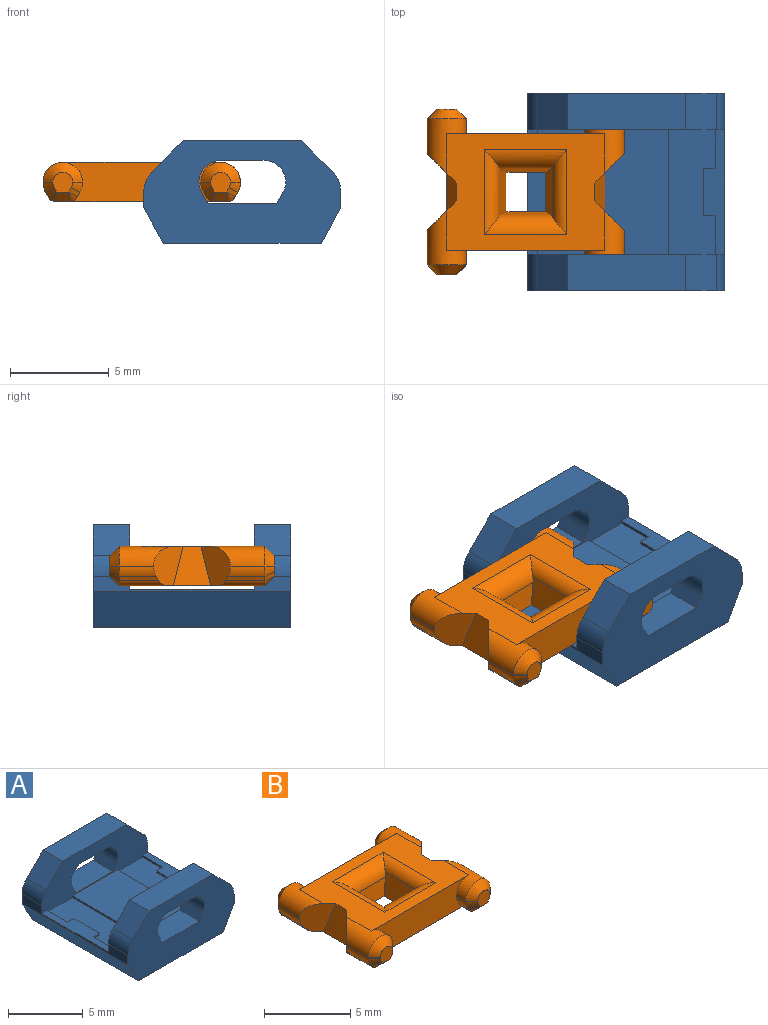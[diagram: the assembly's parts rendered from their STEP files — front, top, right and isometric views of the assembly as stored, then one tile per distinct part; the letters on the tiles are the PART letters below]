
ASSEMBLY  parts=2 mates=1
PART A: 48 faces, bbox 10x10x5.2 mm
  f0: plane 6.3x4.25mm, normal (0,0,1), area 26.8mm2, adj f4,f5,f38,f41
  f1: plane 6.3x1.1mm, normal (0,0,1), area 4.6mm2, adj f4,f5,f10,f42,f43,f44,f45,f46
  f2: plane 3.48x1.85mm, normal (0,0,1), area 6.4mm2, adj f5,f11,f25,f27
  f3: plane 10x0.78mm, normal (1,0,0), area 3.8mm2, adj f4,f5,f9,f11,f20,f29,f32,f33
  f4: plane 10x3.41mm, normal (0,-1,0), area 20.4mm2, adj f0,f1,f3,f7,f8,f10,f13,f17
  f5: plane 10x3.41mm, normal (0,1,0), area 20.4mm2, adj f0,f1,f2,f3,f6,f10,f14,f15
  f6: cylinder r=1.1mm len=1.85mm, axis (0,-1,0), area 4.2mm2, adj f5,f11,f16,f27
  f7: cylinder r=1.1mm len=1.85mm, axis (0,-1,0), area 4.2mm2, adj f4,f9,f17,f28
  f8: plane 3.48x1.85mm, normal (0,0,1), area 6.4mm2, adj f4,f9,f26,f28
  f9: plane 10x5.2mm, normal (0,1,0), area 37.3mm2, adj f3,f7,f8,f10,f12,f13,f17,f18
  f10: plane 10x0.78mm, normal (-1,0,0), area 3.8mm2, adj f1,f4,f5,f9,f11,f19,f30,f31
  f11: plane 10x5.2mm, normal (0,-1,0), area 37.3mm2, adj f2,f3,f6,f10,f12,f14,f15,f16
  f12: plane 10x8mm, normal (0,0,-1), area 80mm2, adj f9,f11,f19,f20
  f13: plane 6x1.85mm, normal (0,0,1), area 11.1mm2, adj f4,f9,f21,f23
  f14: plane 6x1.85mm, normal (0,0,1), area 11.1mm2, adj f5,f11,f22,f24
  f15: cylinder r=1.1mm len=1.85mm, axis (0,-1,0), area 4.2mm2, adj f5,f11,f16,f25
  f16: plane 2.2x1.85mm, normal (0,0,-1), area 4.1mm2, adj f5,f6,f11,f15
  f17: plane 2.2x1.85mm, normal (0,0,-1), area 4.1mm2, adj f4,f7,f9,f18
  f18: cylinder r=1.1mm len=1.85mm, axis (0,-1,0), area 4.2mm2, adj f4,f9,f17,f26
  f19: plane 10x1.8mm, normal (-0.87,0,-0.49), area 20.6mm2, adj f9,f10,f11,f12
  f20: plane 10x1.8mm, normal (0.87,0,-0.49), area 20.6mm2, adj f3,f9,f11,f12
  f21: plane 1.85x1.56mm, normal (0.71,0,0.71), area 4.1mm2, adj f4,f9,f13,f32
  f22: plane 1.85x1.56mm, normal (0.71,0,0.71), area 4.1mm2, adj f5,f11,f14,f33
  f23: plane 1.85x1.56mm, normal (-0.71,0,0.71), area 4.1mm2, adj f4,f9,f13,f30
  f24: plane 1.85x1.56mm, normal (-0.71,0,0.71), area 4.1mm2, adj f5,f11,f14,f31
  f25: plane 1.85x0.56mm, normal (0.87,0,0.5), area 1.2mm2, adj f2,f5,f11,f15
  f26: plane 1.85x0.56mm, normal (0.87,0,0.5), area 1.2mm2, adj f4,f8,f9,f18
  f27: plane 1.85x0.56mm, normal (-0.87,0,0.5), area 1.2mm2, adj f2,f5,f6,f11
  f28: plane 1.85x0.56mm, normal (-0.87,0,0.5), area 1.2mm2, adj f4,f7,f8,f9
  f29: plane 6.3x1.1mm, normal (0,0,1), area 4.6mm2, adj f3,f4,f5,f34,f35,f36,f37,f39
  f30: cylinder r=1.5mm len=1.85mm, axis (0,-1,0), area 2.2mm2, adj f4,f9,f10,f23
  f31: cylinder r=1.5mm len=1.85mm, axis (0,-1,0), area 2.2mm2, adj f5,f10,f11,f24
  f32: cylinder r=1.5mm len=1.85mm, axis (0,1,0), area 2.2mm2, adj f3,f4,f9,f21
  f33: cylinder r=1.5mm len=1.85mm, axis (0,1,0), area 2.2mm2, adj f3,f5,f11,f22
  f34: plane 0.6x0.15mm, normal (0,-1,0), area 0.1mm2, adj f29,f35,f39,f40
  f35: plane 2.4x0.15mm, normal (-1,0,0), area 0.4mm2, adj f29,f34,f36,f40
  f36: plane 0.6x0.15mm, normal (0,1,0), area 0.1mm2, adj f29,f35,f37,f40
  f37: plane 1.95x0.15mm, normal (-1,0,0), area 0.3mm2, adj f4,f29,f36,f40
  f38: plane 6.3x0.15mm, normal (1,0,0), area 0.9mm2, adj f0,f4,f5,f40
  f39: plane 1.95x0.15mm, normal (-1,0,0), area 0.3mm2, adj f5,f29,f34,f40
  f40: plane 6.3x2.38mm, normal (0,0,1), area 13.5mm2, adj f4,f5,f34,f35,f36,f37,f38,f39
  f41: plane 6.3x0.15mm, normal (-1,0,0), area 0.9mm2, adj f0,f4,f5,f47
  f42: plane 1.95x0.15mm, normal (1,0,0), area 0.3mm2, adj f1,f4,f43,f47
  f43: plane 0.6x0.15mm, normal (0,1,0), area 0.1mm2, adj f1,f42,f44,f47
  f44: plane 2.4x0.15mm, normal (1,0,0), area 0.4mm2, adj f1,f43,f45,f47
  f45: plane 0.6x0.15mm, normal (0,-1,0), area 0.1mm2, adj f1,f44,f46,f47
  f46: plane 1.95x0.15mm, normal (1,0,0), area 0.3mm2, adj f1,f5,f45,f47
  f47: plane 6.3x2.38mm, normal (0,0,1), area 13.5mm2, adj f4,f5,f41,f42,f43,f44,f45,f46
PART B: 98 faces, bbox 10x8.4x2 mm
  f0: plane 8x2mm, normal (0,1,0), area 12.7mm2, adj f2,f3,f10,f14,f20,f21,f24,f25
  f1: plane 8x2mm, normal (0,-1,0), area 12.7mm2, adj f2,f3,f4,f7,f22,f23,f28,f29
  f2: plane 8x5.9mm, normal (0,0,1), area 27.8mm2, adj f0,f1,f16,f17,f18,f19,f20,f21
  f3: plane 8.62x7.4mm, normal (0,0,-1), area 47.3mm2, adj f0,f1,f16,f17,f18,f19,f40,f41
  f4: plane 0.75x0.03mm, normal (1,0,0), area 0mm2, adj f1,f23,f35,f63
  f5: plane 1.75x0.03mm, normal (-1,0,0), area 0.1mm2, adj f18,f23,f36,f67
  f6: plane 1x1mm, normal (0,-1,0), area 0.8mm2, adj f62,f63,f64,f65,f67,f68,f69,f71
  f7: plane 0.75x0.03mm, normal (-1,0,0), area 0mm2, adj f1,f22,f34,f57
  f8: plane 1.75x0.03mm, normal (1,0,0), area 0.1mm2, adj f16,f22,f32,f53
  f9: plane 1x1mm, normal (0,-1,0), area 0.8mm2, adj f52,f53,f54,f55,f57,f58,f59,f61
  f10: plane 0.75x0.03mm, normal (1,0,0), area 0mm2, adj f0,f21,f38,f87
  f11: plane 1.75x0.03mm, normal (-1,0,0), area 0.1mm2, adj f19,f21,f37,f83
  f12: plane 1x1mm, normal (0,1,0), area 0.8mm2, adj f82,f83,f84,f85,f87,f88,f89,f91
  f13: plane 1.75x0.03mm, normal (1,0,0), area 0.1mm2, adj f17,f20,f33,f77
  f14: plane 0.75x0.03mm, normal (-1,0,0), area 0mm2, adj f0,f20,f39,f73
  f15: plane 1x1mm, normal (0,1,0), area 0.8mm2, adj f72,f73,f74,f75,f77,f78,f79,f81
  f16: plane 2x1.5mm, normal (0.71,0.71,0), area 3mm2, adj f2,f3,f8,f22,f31,f32,f47,f48
  f17: plane 2x1.5mm, normal (0.71,-0.71,0), area 3mm2, adj f2,f3,f13,f20,f30,f33,f46,f48
  f18: plane 2x1.5mm, normal (-0.71,0.71,0), area 3mm2, adj f2,f3,f5,f23,f27,f36,f43,f51
  f19: plane 2x1.5mm, normal (-0.71,-0.71,0), area 3mm2, adj f2,f3,f11,f21,f26,f37,f42,f51
  f20: cylinder r=1mm len=2.75mm, axis (0,-1,0), area 4.5mm2, adj f0,f2,f13,f14,f17,f75
  f21: cylinder r=1mm len=2.75mm, axis (0,-1,0), area 4.5mm2, adj f0,f2,f10,f11,f19,f85
  f22: cylinder r=1mm len=2.75mm, axis (0,-1,0), area 4.5mm2, adj f1,f2,f7,f8,f16,f55
  f23: cylinder r=1mm len=2.75mm, axis (0,-1,0), area 4.5mm2, adj f1,f2,f4,f5,f18,f65
  f24: plane 0.75x0.22mm, normal (-0.87,0,-0.5), area 0.2mm2, adj f0,f39,f40,f74
  f25: plane 0.75x0.22mm, normal (0.87,0,-0.5), area 0.2mm2, adj f0,f38,f41,f91
  f26: plane 2.01x0.22mm, normal (-0.87,0,-0.5), area 0.5mm2, adj f19,f37,f42,f84
  f27: plane 2.01x0.22mm, normal (-0.87,0,-0.5), area 0.5mm2, adj f18,f36,f43,f71
  f28: plane 0.75x0.22mm, normal (0.87,0,-0.5), area 0.2mm2, adj f1,f35,f44,f64
  f29: plane 0.75x0.22mm, normal (-0.87,0,-0.5), area 0.2mm2, adj f1,f34,f45,f61
  f30: plane 2.01x0.22mm, normal (0.87,0,-0.5), area 0.5mm2, adj f17,f33,f46,f81
  f31: plane 2.01x0.22mm, normal (0.87,0,-0.5), area 0.5mm2, adj f16,f32,f47,f54
  f32: cylinder r=1mm len=1.88mm, axis (0,1,0), area 0.9mm2, adj f8,f16,f31,f52
  f33: cylinder r=1mm len=1.88mm, axis (0,1,0), area 0.9mm2, adj f13,f17,f30,f79
  f34: cylinder r=1mm len=0.75mm, axis (0,-1,0), area 0.4mm2, adj f1,f7,f29,f59
  f35: cylinder r=1mm len=0.75mm, axis (0,1,0), area 0.4mm2, adj f1,f4,f28,f62
  f36: cylinder r=1mm len=1.88mm, axis (0,-1,0), area 0.9mm2, adj f5,f18,f27,f69
  f37: cylinder r=1mm len=1.88mm, axis (0,-1,0), area 0.9mm2, adj f11,f19,f26,f82
  f38: cylinder r=1mm len=0.75mm, axis (0,1,0), area 0.4mm2, adj f0,f10,f25,f89
  f39: cylinder r=1mm len=0.75mm, axis (0,-1,0), area 0.4mm2, adj f0,f14,f24,f72
  f40: cylinder r=0.5mm len=0.75mm, axis (0,-1,0), area 0.4mm2, adj f0,f3,f24,f76
  f41: cylinder r=0.5mm len=0.75mm, axis (0,-1,0), area 0.4mm2, adj f0,f3,f25,f90
  f42: cylinder r=0.5mm len=2.44mm, axis (0,-1,0), area 1.2mm2, adj f3,f19,f26,f86
  f43: cylinder r=0.5mm len=2.44mm, axis (0,1,0), area 1.2mm2, adj f3,f18,f27,f70
  f44: cylinder r=0.5mm len=0.75mm, axis (0,1,0), area 0.4mm2, adj f1,f3,f28,f66
  f45: cylinder r=0.5mm len=0.75mm, axis (0,1,0), area 0.4mm2, adj f1,f3,f29,f60
  f46: cylinder r=0.5mm len=2.44mm, axis (0,-1,0), area 1.2mm2, adj f3,f17,f30,f80
  f47: cylinder r=0.5mm len=2.44mm, axis (0,1,0), area 1.2mm2, adj f3,f16,f31,f56
  f48: plane 2x1.9mm, normal (0.97,0,0.24), area 2.9mm2, adj f2,f3,f16,f17
  f49: plane 2.52x1.43mm, normal (-0.97,0,0.24), area 3.3mm2, adj f3,f92,f93,f94,f96,f97
  f50: plane 2.52x1.43mm, normal (0.97,0,0.24), area 3.3mm2, adj f3,f92,f93,f95,f96,f97
  f51: plane 2x1.9mm, normal (-0.97,0,0.24), area 2.9mm2, adj f2,f3,f18,f19
  f52: cone r=0.5mm half-angle=45deg, axis (0,1,0), area 0.3mm2, adj f9,f32,f53,f54
  f53: plane 0.5x0.5mm, normal (0.71,-0.71,0), area 0mm2, adj f8,f9,f52,f55
  f54: plane 0.56x0.5mm, normal (0.61,-0.71,-0.35), area 0.2mm2, adj f9,f31,f52,f56
  f55: cone r=0.5mm half-angle=45deg, axis (0,1,0), area 1.7mm2, adj f9,f22,f53,f57
  f56: cone r=0.5mm half-angle=45deg, axis (0,1,0), area 0.2mm2, adj f47,f54,f58
  f57: plane 0.5x0.5mm, normal (-0.71,-0.71,0), area 0mm2, adj f7,f9,f55,f59
  f58: plane 0.62x0.5mm, normal (0,-0.71,-0.71), area 0.4mm2, adj f3,f9,f56,f60
  f59: cone r=0.5mm half-angle=45deg, axis (0,1,0), area 0.3mm2, adj f9,f34,f57,f61
  f60: cone r=0.5mm half-angle=45deg, axis (0,1,0), area 0.2mm2, adj f45,f58,f61
  f61: plane 0.56x0.5mm, normal (-0.61,-0.71,-0.35), area 0.2mm2, adj f9,f29,f59,f60
  f62: cone r=0.5mm half-angle=45deg, axis (0,1,0), area 0.3mm2, adj f6,f35,f63,f64
  f63: plane 0.5x0.5mm, normal (0.71,-0.71,0), area 0mm2, adj f4,f6,f62,f65
  f64: plane 0.56x0.5mm, normal (0.61,-0.71,-0.35), area 0.2mm2, adj f6,f28,f62,f66
  f65: cone r=0.5mm half-angle=45deg, axis (0,1,0), area 1.7mm2, adj f6,f23,f63,f67
  f66: cone r=0.5mm half-angle=45deg, axis (0,1,0), area 0.2mm2, adj f44,f64,f68
  f67: plane 0.5x0.5mm, normal (-0.71,-0.71,0), area 0mm2, adj f5,f6,f65,f69
  f68: plane 0.62x0.5mm, normal (0,-0.71,-0.71), area 0.4mm2, adj f3,f6,f66,f70
  f69: cone r=0.5mm half-angle=45deg, axis (0,1,0), area 0.3mm2, adj f6,f36,f67,f71
  f70: cone r=0.5mm half-angle=45deg, axis (0,1,0), area 0.2mm2, adj f43,f68,f71
  f71: plane 0.56x0.5mm, normal (-0.61,-0.71,-0.35), area 0.2mm2, adj f6,f27,f69,f70
  f72: cone r=0.5mm half-angle=45deg, axis (0,-1,0), area 0.3mm2, adj f15,f39,f73,f74
  f73: plane 0.5x0.5mm, normal (-0.71,0.71,0), area 0mm2, adj f14,f15,f72,f75
  f74: plane 0.56x0.5mm, normal (-0.61,0.71,-0.35), area 0.2mm2, adj f15,f24,f72,f76
  f75: cone r=0.5mm half-angle=45deg, axis (0,-1,0), area 1.7mm2, adj f15,f20,f73,f77
  f76: cone r=0.5mm half-angle=45deg, axis (0,-1,0), area 0.2mm2, adj f40,f74,f78
  f77: plane 0.5x0.5mm, normal (0.71,0.71,0), area 0mm2, adj f13,f15,f75,f79
  f78: plane 0.62x0.5mm, normal (0,0.71,-0.71), area 0.4mm2, adj f3,f15,f76,f80
  f79: cone r=0.5mm half-angle=45deg, axis (0,-1,0), area 0.3mm2, adj f15,f33,f77,f81
  f80: cone r=0.5mm half-angle=45deg, axis (0,-1,0), area 0.2mm2, adj f46,f78,f81
  f81: plane 0.56x0.5mm, normal (0.61,0.71,-0.35), area 0.2mm2, adj f15,f30,f79,f80
  f82: cone r=0.5mm half-angle=45deg, axis (0,-1,0), area 0.3mm2, adj f12,f37,f83,f84
  f83: plane 0.5x0.5mm, normal (-0.71,0.71,0), area 0mm2, adj f11,f12,f82,f85
  f84: plane 0.56x0.5mm, normal (-0.61,0.71,-0.35), area 0.2mm2, adj f12,f26,f82,f86
  f85: cone r=0.5mm half-angle=45deg, axis (0,-1,0), area 1.7mm2, adj f12,f21,f83,f87
  f86: cone r=0.5mm half-angle=45deg, axis (0,-1,0), area 0.2mm2, adj f42,f84,f88
  f87: plane 0.5x0.5mm, normal (0.71,0.71,0), area 0mm2, adj f10,f12,f85,f89
  f88: plane 0.62x0.5mm, normal (0,0.71,-0.71), area 0.4mm2, adj f3,f12,f86,f90
  f89: cone r=0.5mm half-angle=45deg, axis (0,-1,0), area 0.3mm2, adj f12,f38,f87,f91
  f90: cone r=0.5mm half-angle=45deg, axis (0,-1,0), area 0.2mm2, adj f41,f88,f91
  f91: plane 0.56x0.5mm, normal (0.61,0.71,-0.35), area 0.2mm2, adj f12,f25,f89,f90
  f92: plane 2.57x1.15mm, normal (0,0.99,0.15), area 2.7mm2, adj f3,f49,f50,f96
  f93: plane 2.57x1.15mm, normal (0,-0.99,0.15), area 2.7mm2, adj f3,f49,f50,f97
  f94: cylinder r=0.75mm len=4.32mm, axis (0,1,0), area 3.3mm2, adj f2,f49,f96,f97
  f95: cylinder r=0.75mm len=4.32mm, axis (0,1,0), area 3.3mm2, adj f2,f50,f96,f97
  f96: cylinder r=1mm len=4.17mm, axis (-1,0,0), area 4.5mm2, adj f2,f49,f50,f92,f94,f95
  f97: cylinder r=1mm len=4.17mm, axis (-1,0,0), area 4.5mm2, adj f2,f49,f50,f93,f94,f95
PLACE A t=(-2.45,1.46,0.9)mm fixed
PLACE B t=(-7.55,1.46,3)mm
MATE revolute A.f15 <-> B.f20  axis (0,-1,0) through (-3.55,-3.54,4)mm
